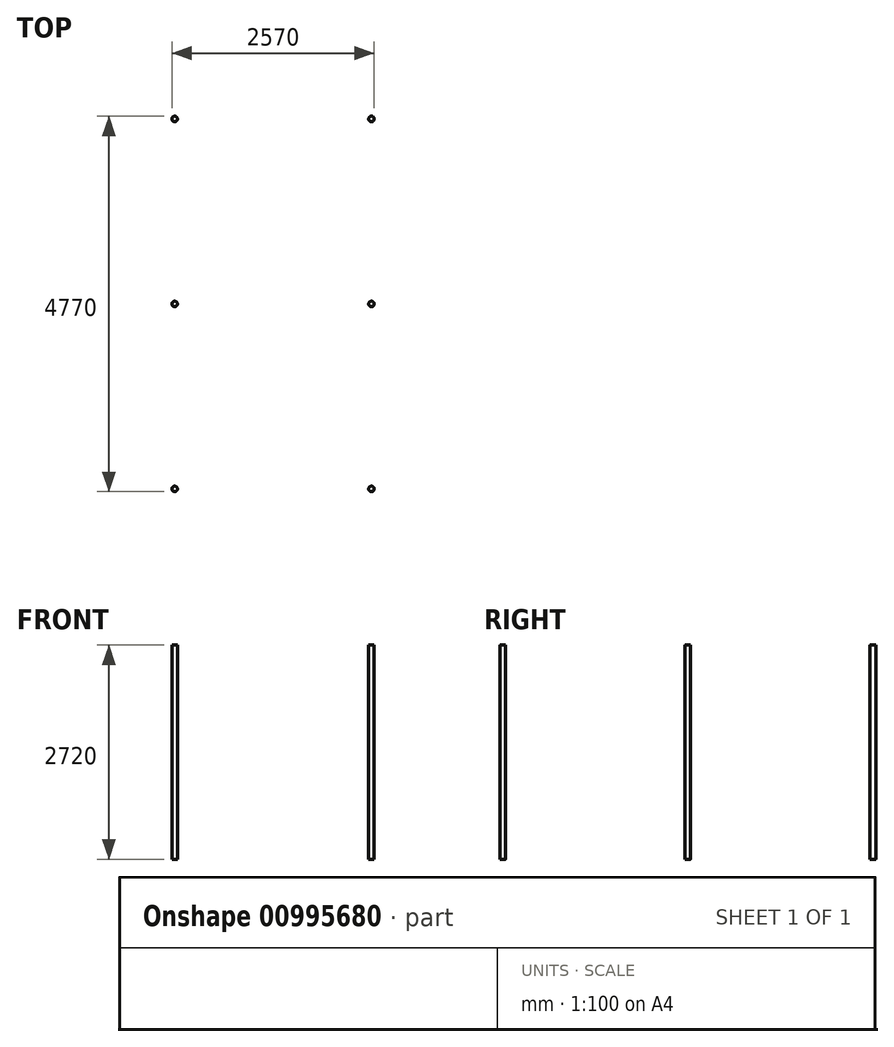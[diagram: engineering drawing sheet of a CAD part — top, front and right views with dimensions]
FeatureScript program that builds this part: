
annotation { "Feature Type Name" : "Feature", "Feature Type Description" : "" }
export const myFeature = defineFeature(function(context is Context, id is Id, definition is map)
    precondition{}
    {
        {
            var Q0;
            Q0=qCreatedBy(makeId("Right.planeOp"),FACE);
            var sketch = newSketch(context, id + "F0", { "sketchPlane" : qUnion([Q0])});
            skLineSegment(sketch, "E0", {"start": v(0, 0) * mm, "end": v(5000, 0) * mm, "construction": true});
            skLineSegment(sketch, "E1", {"start": v(5000, 0) * mm, "end": v(5000, 2611.63) * mm, "construction": true});
            skLineSegment(sketch, "E2", {"start": v(5000, 2611.63) * mm, "end": v(0, 1730) * mm, "construction": true});
            skLineSegment(sketch, "E3", {"start": v(0, 1730) * mm, "end": v(0, 0) * mm, "construction": true});
            skLineSegment(sketch, "E4", {"start": v(150, 1756.45) * mm, "end": v(150, 0) * mm, "construction": true});
            skLineSegment(sketch, "E5", {"start": v(2500, 2170.82) * mm, "end": v(2500, 0) * mm, "construction": true});
            skLineSegment(sketch, "E6", {"start": v(4850, 2585.19) * mm, "end": v(4850, 0) * mm, "construction": true});
            skSolve(sketch);
        }
        {
            var Q0;
            Q0=qCreatedBy(makeId("Top.planeOp"),FACE);
            var sketch = newSketch(context, id + "F1", { "sketchPlane" : qUnion([Q0])});
            skLineSegment(sketch, "E7.bottom", {"start": v(0, 0) * mm, "end": v(2500, 0) * mm, "construction": true});
            skLineSegment(sketch, "E7.top", {"start": v(0, 5000) * mm, "end": v(2500, 5000) * mm, "construction": true});
            skLineSegment(sketch, "E7.left", {"start": v(0, 0) * mm, "end": v(0, 5000) * mm, "construction": true});
            skLineSegment(sketch, "E7.right", {"start": v(2500, 0) * mm, "end": v(2500, 5000) * mm, "construction": true});
            skPoint(sketch, "E7.middle", {"position": v(1250, 2500) * mm});
            skLineSegment(sketch, "E8", {"start": v(0, 4850) * mm, "end": v(2500, 4850) * mm, "construction": true});
            skLineSegment(sketch, "E9", {"start": v(0, 2500) * mm, "end": v(2500, 2500) * mm, "construction": true});
            skLineSegment(sketch, "E10", {"start": v(0, 150) * mm, "end": v(2500, 150) * mm, "construction": true});
            skCircle(sketch, "E11", {"center": v(0, 4850) * mm, "radius": 35 * mm});
            skCircle(sketch, "E12", {"center": v(0, 2500) * mm, "radius": 35 * mm});
            skCircle(sketch, "E13", {"center": v(0, 150) * mm, "radius": 35 * mm});
            skLineSegment(sketch, "E14", {"start": v(1250, 5000) * mm, "end": v(1250, 0) * mm, "construction": true});
            skCircle(sketch, "E15", {"center": v(2500, 150) * mm, "radius": 35 * mm});
            skCircle(sketch, "E16", {"center": v(2500, 4850) * mm, "radius": 35 * mm});
            skCircle(sketch, "E17", {"center": v(2500, 2500) * mm, "radius": 35 * mm});
            skSolve(sketch);
        }
        {
            var Q0;
            Q0 = qSketchRegion(id + "F1", true);
            var Q1;
            Q1 = qBodyType(qCreatedBy(id + "F1" ,EDGE), BodyType.WIRE);
            extrude(context, id + "F2", {"entities" : qUnion([Q0]), "bodyType" : ToolBodyType.SURFACE, "surfaceEntities" : qUnion([Q1]), "depth" : 2720 * mm, "offsetDistance" : 25 * mm});
        }
    });
